annotation { "Feature Type Name" : "Feature", "Feature Type Description" : "" }
export const myFeature = defineFeature(function(context is Context, id is Id, definition is map)
    precondition{}
    {
        {
            var Q0;
            Q0=qCreatedBy(makeId("Front.planeOp"),FACE);
            var sketch = newSketch(context, id + "F0", { "sketchPlane" : qUnion([Q0])});
            skLineSegment(sketch, "E0.bottom", {"start": v(0, 0) * mm, "end": v(450, 0) * mm, "construction": true});
            skLineSegment(sketch, "E0.top", {"start": v(0, 200) * mm, "end": v(450, 200) * mm, "construction": true});
            skLineSegment(sketch, "E0.left", {"start": v(0, 0) * mm, "end": v(0, 200) * mm, "construction": true});
            skLineSegment(sketch, "E0.right", {"start": v(450, 0) * mm, "end": v(450, 200) * mm, "construction": true});
            skText(sketch, "E1", { "text": "Keith Kitson\n", "fontName": "OpenSans-Regular.ttf"});
            skLineSegment(sketch, "E2", {"start": v(225, 141.66) * mm, "end": v(225, 126.66) * mm, "construction": true});
            skLineSegment(sketch, "E3", {"start": v(225, 126.66) * mm, "end": v(143.33, 126.66) * mm, "construction": true});
            skLineSegment(sketch, "E4", {"start": v(0, 200) * mm, "end": v(-43.81, 200) * mm, "construction": true});
            skLineSegment(sketch, "E5", {"start": v(-43.81, 200) * mm, "end": v(-43.81, 141.66) * mm, "construction": true});
            skLineSegment(sketch, "E6.MirrorCS", {"start": v(450, 200) * mm, "end": v(493.81, 200) * mm, "construction": true});
            skLineSegment(sketch, "E7.MirrorCS", {"start": v(493.81, 200) * mm, "end": v(493.81, 141.66) * mm, "construction": true});
            skLineSegment(sketch, "E8.MirrorCS", {"start": v(-43.81, 53.31) * mm, "end": v(-43.81, 111.66) * mm, "construction": true});
            skLineSegment(sketch, "E9.MirrorCS", {"start": v(493.81, 53.31) * mm, "end": v(493.81, 111.66) * mm, "construction": true});
            skLineSegment(sketch, "E10.MirrorCS", {"start": v(450, 53.31) * mm, "end": v(493.81, 53.31) * mm, "construction": true});
            skLineSegment(sketch, "E11.MirrorCS", {"start": v(0, 53.31) * mm, "end": v(-43.81, 53.31) * mm, "construction": true});
            skLineSegment(sketch, "E12", {"start": v(-43.81, 111.66) * mm, "end": v(493.81, 111.66) * mm, "construction": true});
            skText(sketch, "E13", { "text": "Tunnel 2017", "fontName": "OpenSans-Regular.ttf"});
            const initialGuessF0  = {"E1": [0, 0.14166, 1, 0, 0.05834], "E13": [0, 0.05331, 1, 0, 0.05637]};
            skSetInitialGuess(sketch, initialGuessF0);
            skSolve(sketch);
        }
        {
            var Q0;
            Q0 = qSketchRegion(id + "F0", true);
            extrude(context, id + "F1", {"entities" : qUnion([Q0]), "depth" : 5 * mm});
        }
    });